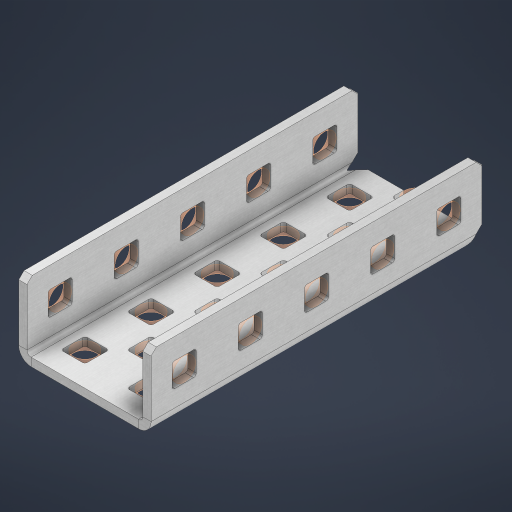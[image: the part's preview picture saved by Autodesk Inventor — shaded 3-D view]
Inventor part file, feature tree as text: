
AUTODESK INVENTOR PART (.ipt)
format: ipt  version: 2023 (Build 270158000, 158)  size: 716,288 bytes
history: native  units: in
note: dims shown in document units (in); Inventor stores cm internally (conversion verified against a paired STEP export)
features: other x32, extrude x23, sheet_metal_op x11, sketch x10, pattern_linear x2, mirror x1, chamfer x1
ambient origin geometry x8: Origin, YZ Plane, XZ Plane, XY Plane, X Axis, Y Axis, Z Axis, Center Point
bodies: Solid1 (feature_tree), Body (feature_tree)
feature tree (80):
  sheet_metal_op  "Flanges"
  other  "Flange Pattern Plane"
  other  "Flange Pattern Sketch"
  sheet_metal_op  "Flange Pattern"
  sheet_metal_op  "Body Pattern"
  pattern_linear  "Center Pattern"  Spacing1=0.0625in  [1 undecoded]
  other  "Arc Length"
  mirror  "Notch Mirror"
  pattern_linear  "Notch Pattern"  Spacing1=0.182in  [1 undecoded]
  chamfer  "End Chamfer"
  extrude  "Half Cut"  Depth=0.02in
  sketch  "Sketch1"  dims[d0=1.0in]
  other  "Plate1"
  sketch  "Sketch2"  dims[d1=2.5in]
  other  "Plate2"
  sheet_metal_op  "Bend1"
  sheet_metal_op  "Corner1"
  sketch  "Sketch3"  dims[d2=0.0625in]
  sketch  "Sketch7"  dims[d3=0.0625in]
  other  "Srf1"
  other  "Srf2"
  sketch  "Sketch8"  dims[d4=0.0312in]
  sketch  "Sketch9"  dims[d5=0.125in]
  other  "Srf91"
  sheet_metal_op  "Body Pattern Sketch"
  other  "Srf92"
  sketch  "Sketch13"  dims[d6=0.0625in]
  sketch  "Sketch14"  dims[d7=0.5in d8=90.0deg d9=0.0312in]
  sketch  "Sketch15"  dims[d10=0.25in]
  sketch  "Sketch16"  dims[d11=0.0625in d12=0.0625in d16=0.182in d17=0.02in d18=0.0625in d19=0.0in d20=0.25in d21=0.25in d38=1.9685in d40=0.5in d41=0.7874in d43=1.0in d46=0.172in d47=1.0in d48=0.0in d49=0.182in d50=0.02in d51=0.25in d52=0.25in d53=0.0625in d54=0.0in d55=0.172in d56=1.0in d57=0.0in d58=0.25in d60=1.9685in d62=0.5in d63=0.7874in d65=0.5in d85=0.1473in d86=0.1782in d88=0.04in d89=0.0625in d90=0.0in d91=0.04in d92=0.0491in d95=2.5in d96=0.04in d97=0.25in d98=45.0deg d99=0.25in d100=0.5in d101=0.0in d102=2.497in d106=0.182in d107=0.02in d108=0.5in d109=0.5in d110=0.0625in d111=0.0in d112=0.172in d113=0.5in d114=0.0in d117=0.5in d118=0.5in d119=0.5in]
  other  "Srf786"
  other  "Srf823"
  other  "Srf824"
  other  "Srf825"
  other  "Srf826"
  other  "Srf827"
  other  "Srf828"
  other  "Srf829"
  other  "Srf856"
  other  "Srf857"
  other  "Srf858"
  other  "Srf859"
  other  "Srf860"
  other  "Srf861"
  other  "Srf862"
  other  "Srf889"
  other  "Srf890"
  other  "Srf891"
  other  "Srf892"
  other  "Srf922"
  other  "Srf959"
  sheet_metal_op  "Flange Stamp"
  sheet_metal_op  "Flange Circle"
  sheet_metal_op  "Body Stamp"
  sheet_metal_op  "Body Circle"
  other  "Center Stamp"
  other  "Center Circle"
  sheet_metal_op  "Notch"
  extrude  "ExtrusionSrf2"  Depth=0.0625in
  extrude  "ExtrusionSrf92"  TaperAngle=0.0deg  [1 undecoded]
  extrude  "ExtrusionSrf823"  Depth=0.5in
  extrude  "ExtrusionSrf824"  Depth=0.5in
  extrude  "ExtrusionSrf825"  Depth=0.5in
  extrude  "ExtrusionSrf826"  Depth=0.5in
  extrude  "ExtrusionSrf827"  Depth=1.0in TaperAngle=0.0deg
  extrude  "ExtrusionSrf828"  Depth=0.5in
  extrude  "ExtrusionSrf829"  Depth=0.02in
  extrude  "ExtrusionSrf856"  Depth=0.5in
  extrude  "ExtrusionSrf857"  Depth=0.5in
  extrude  "ExtrusionSrf858"  Depth=0.0625in
  extrude  "ExtrusionSrf859"  TaperAngle=0.0deg  [1 undecoded]
  extrude  "ExtrusionSrf860"  Depth=0.5in
  extrude  "ExtrusionSrf861"  Depth=1.0in TaperAngle=0.0deg
  extrude  "ExtrusionSrf862"  Depth=0.5in
  extrude  "ExtrusionSrf889"  Depth=0.5in
  extrude  "ExtrusionSrf890"  Depth=0.5in
  extrude  "ExtrusionSrf891"  Depth=0.5in
  extrude  "ExtrusionSrf892"  Depth=0.5in
  extrude  "ExtrusionSrf922"  Depth=0.5in
  extrude  "ExtrusionSrf959"  Depth=0.0625in
note: 4 required parameter values undecoded (feature->parameter linkage not recoverable at this tier; creation-order binding heuristic only, values carry confidence <= 0.55)
